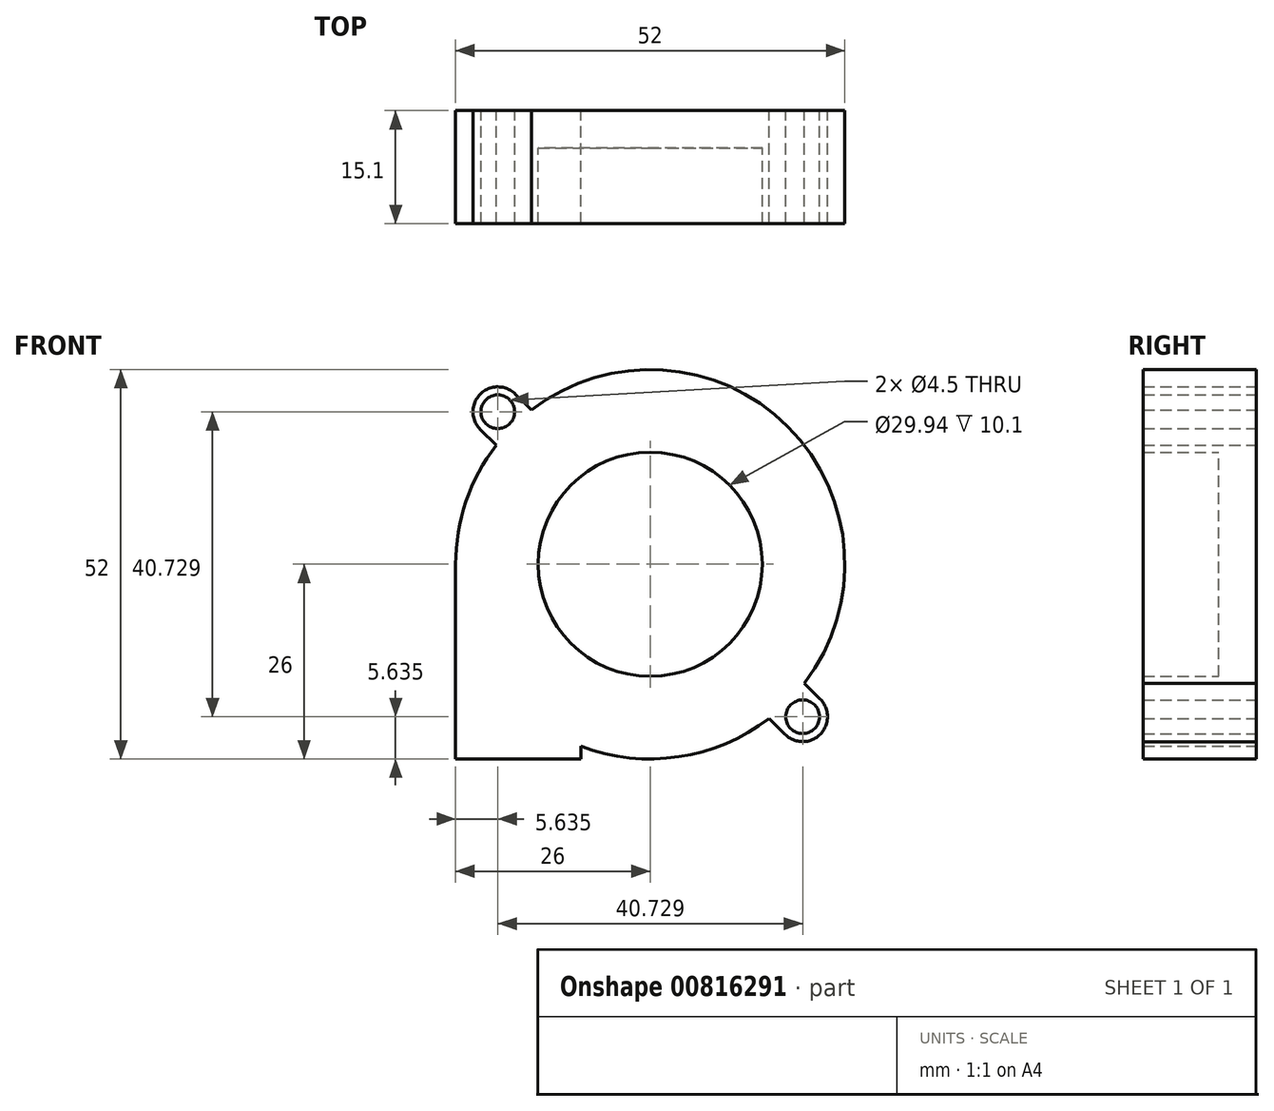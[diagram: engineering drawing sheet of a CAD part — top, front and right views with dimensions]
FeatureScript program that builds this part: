
annotation { "Feature Type Name" : "Feature", "Feature Type Description" : "" }
export const myFeature = defineFeature(function(context is Context, id is Id, definition is map)
    precondition{}
    {
        {
            var Q0;
            Q0=qCreatedBy(makeId("Front.planeOp"),FACE);
            var sketch = newSketch(context, id + "F0", { "sketchPlane" : qUnion([Q0])});
            skCircle(sketch, "E0", {"center": v(0, 0) * mm, "radius": 26 * mm});
            skCircle(sketch, "E1", {"center": v(20.36, -20.36) * mm, "radius": 2.25 * mm});
            skCircle(sketch, "E2", {"center": v(-20.36, 20.36) * mm, "radius": 2.25 * mm});
            skLineSegment(sketch, "E3", {"start": v(0, 0) * mm, "end": v(0, 1) * mm, "construction": true});
            skLineSegment(sketch, "E4", {"start": v(0, 1) * mm, "end": v(-1, 1) * mm, "construction": true});
            skLineSegment(sketch, "E5", {"start": v(0, 0) * mm, "end": v(-1, 1) * mm, "construction": true});
            skLineSegment(sketch, "E6", {"start": v(20.36, -20.36) * mm, "end": v(-20.36, 20.36) * mm, "construction": true});
            skCircle(sketch, "E7", {"center": v(-20.36, 20.36) * mm, "radius": 3.33 * mm});
            skCircle(sketch, "E8", {"center": v(20.36, -20.36) * mm, "radius": 3.33 * mm});
            skLineSegment(sketch, "E9", {"start": v(-26, 0) * mm, "end": v(-26, -26) * mm});
            skPoint(sketch, "E10", {"position": v(0, -26) * mm});
            skLineSegment(sketch, "E11", {"start": v(-26, -26) * mm, "end": v(-9.25, -26) * mm});
            skLineSegment(sketch, "E12", {"start": v(-9.25, -26) * mm, "end": v(-9.25, -24.3) * mm});
            skLineSegment(sketch, "E13", {"start": v(-22.7, 18) * mm, "end": v(-20.58, 15.88) * mm});
            skLineSegment(sketch, "E14", {"start": v(-18, 22.7) * mm, "end": v(-15.88, 20.58) * mm});
            skLineSegment(sketch, "E15", {"start": v(22.7, -18) * mm, "end": v(20.58, -15.88) * mm});
            skLineSegment(sketch, "E16", {"start": v(15.88, -20.58) * mm, "end": v(18, -22.7) * mm});
            skCircle(sketch, "E17", {"center": v(0, 0) * mm, "radius": 14.97 * mm});
            skSolve(sketch);
        }
        {
            var Q0;
            Q0 = qSketchRegion(id + "F0", true);
            var Q1;
            {var subQ0=sQuery(id+"F0.wireOp",EDGE,"E7");var subQ1=sQuery(id+"F0.wireOp",EDGE,"E0");var subQ2=makeQuery(id+"F0.imprint","INTERSECT",VERTEX,{"disambiguationData":[OD(0.0)],"derivedFrom":[subQ1,subQ0]});Q1=makeQuery(id+"F0.imprint","IMPRINT",FACE,{"disambiguationData":[TD([[makeQuery(id+"F0.imprint","IMPRINT",EDGE,{"disambiguationData":[TD([[subQ2,-1.0]])],"derivedFrom":subQ1}),1.0]])]});}
            var Q2;
            {var subQ0=sQuery(id+"F0.wireOp",EDGE,"E8");var subQ1=sQuery(id+"F0.wireOp",EDGE,"E0");var subQ2=makeQuery(id+"F0.imprint","INTERSECT",VERTEX,{"disambiguationData":[OD(0.0)],"derivedFrom":[subQ1,subQ0]});Q2=makeQuery(id+"F0.imprint","IMPRINT",FACE,{"disambiguationData":[TD([[makeQuery(id+"F0.imprint","IMPRINT",EDGE,{"disambiguationData":[TD([[subQ2,-1.0]])],"derivedFrom":subQ1}),1.0]])]});}
            extrude(context, id + "F1", {"entities" : qUnion([Q0, Q1, Q2]), "depth" : 15.1 * mm, "offsetDistance" : 25 * mm});
        }
        {
            var Q0;
            Q0=makeQuery(id+"F0.imprint","IMPRINT",FACE,{"disambiguationData":[TD([[makeQuery(id+"F0.imprint","IMPRINT",EDGE,{"derivedFrom":sQuery(id+"F0.wireOp",EDGE,"E17")}),1.0]])]});
            extrude(context, id + "F2", {"entities" : qUnion([Q0]), "operationType" : NewBodyOperationType.ADD, "depth" : 5 * mm, "offsetDistance" : 25 * mm});
        }
    });
